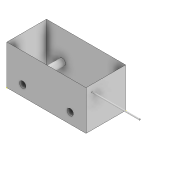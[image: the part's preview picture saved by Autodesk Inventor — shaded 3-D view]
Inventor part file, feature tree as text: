
AUTODESK INVENTOR PART (.ipt)
format: ipt  version: 2022 (Build 260153000, 153)  size: 105,472 bytes
history: native  units: mm
features: sketch x5, extrude x3, delete_face x1, projected_geometry x1
ambient origin geometry x8: Origin, YZ Plane, XZ Plane, XY Plane, X Axis, Y Axis, Z Axis, Center Point
bodies: Solid1 (feature_tree), Solid2 (feature_tree)
feature tree (10):
  extrude  "Extrusion1"  Depth=150.0mm
  sketch  "Sketch2"  dims[d2=150.0mm d3=0.0mm d4=24.0mm]
  extrude  "Extrusion2"  Depth=150.0mm
  delete_face  "Delete Face1"
  sketch  "Sketch4"  dims[d7=24.0mm]
  extrude  "Extrusion3"  Depth=60.0mm
  sketch  "Sketch1"  dims[d0=300.0mm d1=150.0mm]
  sketch  "Sketch3"  dims[d5=40.0mm d6=60.0mm]
  projected_geometry  "Projected Loop1"
  sketch  "Sketch5"  dims[d8=60.0mm d9=150.0mm d10=0.0mm d11=5.0mm d12=180.0mm d13=0.0mm]
